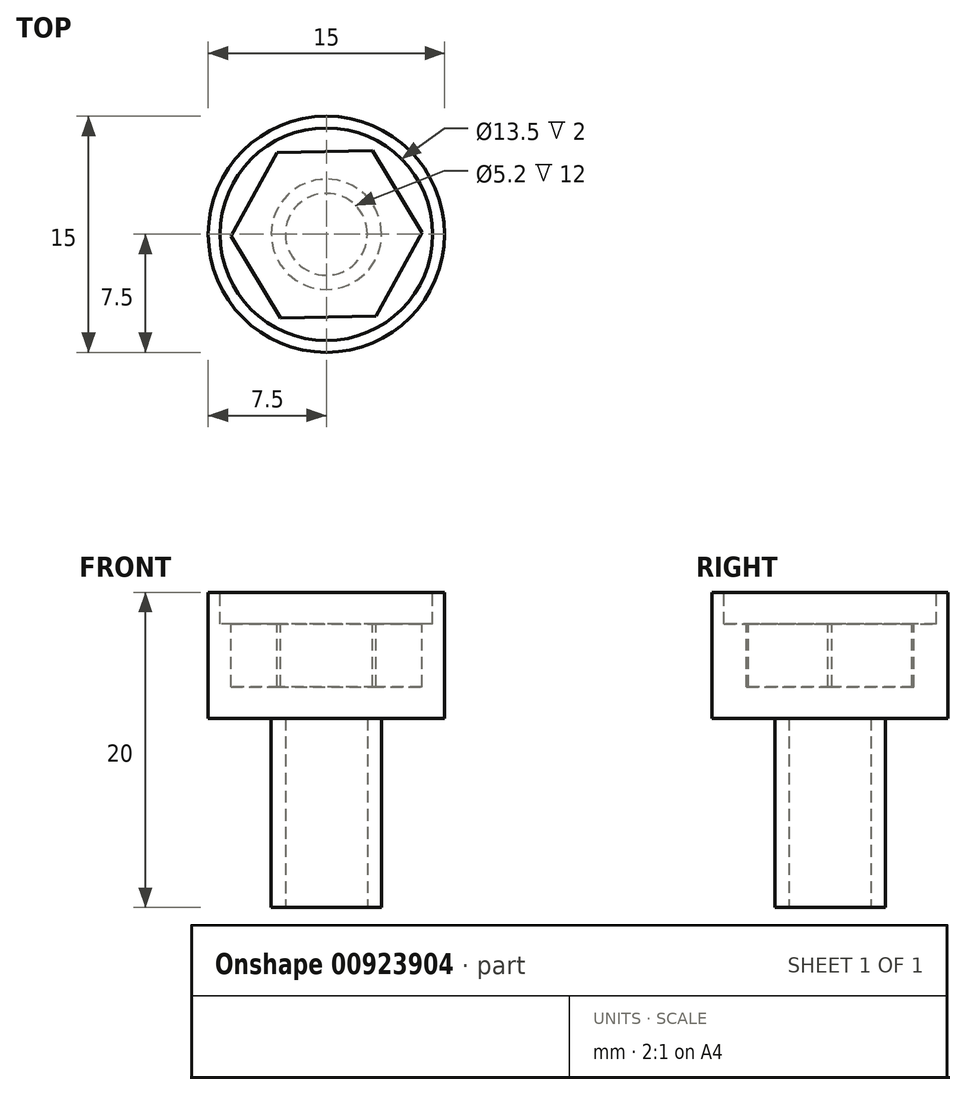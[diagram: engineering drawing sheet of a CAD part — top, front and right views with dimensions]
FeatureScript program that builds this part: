
annotation { "Feature Type Name" : "Feature", "Feature Type Description" : "" }
export const myFeature = defineFeature(function(context is Context, id is Id, definition is map)
    precondition{}
    {
        {
            var Q0;
            Q0=qCreatedBy(makeId("Top.planeOp"),FACE);
            var sketch = newSketch(context, id + "F0", { "sketchPlane" : qUnion([Q0])});
            skCircle(sketch, "E0", {"center": v(0, 0) * mm, "radius": 7.5 * mm});
            skSolve(sketch);
        }
        {
            var Q0;
            Q0=makeQuery(id+"F0.imprint","IMPRINT",FACE,{"disambiguationData":[TD([[makeQuery(id+"F0.imprint","IMPRINT",EDGE,{"derivedFrom":sQuery(id+"F0.wireOp",EDGE,"E0")}),1.0]])]});
            extrude(context, id + "F1", {"entities" : qUnion([Q0]), "depth" : 8 * mm, "offsetDistance" : 25 * mm});
        }
        {
            var Q0;
            Q0=makeQuery(id+"F1.opExtrude","CAP_FACE",FACE,{"disambiguationData":[OSD([sQuery(id+"F0.wireOp",EDGE,"E0")])],"isStart":false});
            var sketch = newSketch(context, id + "F2", { "sketchPlane" : qUnion([Q0])});
            skCircle(sketch, "E1", {"center": v(0, 0) * mm, "radius": 6.75 * mm});
            skSolve(sketch);
        }
        {
            var Q0;
            Q0=makeQuery(id+"F2.imprint","IMPRINT",FACE,{"disambiguationData":[TD([[makeQuery(id+"F2.imprint","IMPRINT",EDGE,{"derivedFrom":sQuery(id+"F2.wireOp",EDGE,"E1")}),1.0]])]});
            extrude(context, id + "F3", {"entities" : qUnion([Q0]), "operationType" : NewBodyOperationType.REMOVE, "oppositeDirection" : true, "depth" : 2 * mm, "offsetDistance" : 25 * mm});
        }
        {
            var Q0;
            Q0=makeQuery(id+"F3.boolean.opBoolean","COPY",FACE,{"derivedFrom":makeQuery(id+"F3.opExtrude","CAP_FACE",FACE,{"disambiguationData":[OSD([sQuery(id+"F2.wireOp",EDGE,"E1")])],"isStart":false})});
            var sketch = newSketch(context, id + "F4", { "sketchPlane" : qUnion([Q0])});
            skCircle(sketch, "E2.cCircle", {"center": v(0, 0) * mm, "radius": 5.25 * mm, "construction": true});
            skLineSegment(sketch, "E2.0", {"start": v(2.92, 5.31) * mm, "end": v(6.06, 0.12) * mm});
            skLineSegment(sketch, "E2.1", {"start": v(6.06, 0.12) * mm, "end": v(3.14, -5.19) * mm});
            skLineSegment(sketch, "E2.2", {"start": v(3.14, -5.19) * mm, "end": v(-2.92, -5.31) * mm});
            skLineSegment(sketch, "E2.3", {"start": v(-2.92, -5.31) * mm, "end": v(-6.06, -0.12) * mm});
            skLineSegment(sketch, "E2.4", {"start": v(-6.06, -0.12) * mm, "end": v(-3.14, 5.19) * mm});
            skLineSegment(sketch, "E2.5", {"start": v(-3.14, 5.19) * mm, "end": v(2.92, 5.31) * mm});
            skPoint(sketch, "E2.0.midPoint", {"position": v(4.5, 2.72) * mm});
            skSolve(sketch);
        }
        {
            var Q0;
            Q0=makeQuery(id+"F4.imprint","IMPRINT",FACE,{"disambiguationData":[TD([[makeQuery(id+"F4.imprint","IMPRINT",EDGE,{"derivedFrom":sQuery(id+"F4.wireOp",EDGE,"E2.0")}),-1.0]])]});
            extrude(context, id + "F5", {"entities" : qUnion([Q0]), "operationType" : NewBodyOperationType.REMOVE, "oppositeDirection" : true, "depth" : 4 * mm, "offsetDistance" : 25 * mm});
        }
        {
            var Q0;
            Q0=makeQuery(id+"F1.opExtrude","CAP_FACE",FACE,{"disambiguationData":[OSD([sQuery(id+"F0.wireOp",EDGE,"E0")])],"isStart":true});
            var sketch = newSketch(context, id + "F6", { "sketchPlane" : qUnion([Q0])});
            skCircle(sketch, "E3", {"center": v(0, 0) * mm, "radius": 3.5 * mm});
            skSolve(sketch);
        }
        {
            var Q0;
            Q0=makeQuery(id+"F6.imprint","IMPRINT",FACE,{"disambiguationData":[TD([[makeQuery(id+"F6.imprint","IMPRINT",EDGE,{"derivedFrom":sQuery(id+"F6.wireOp",EDGE,"E3")}),1.0]])]});
            extrude(context, id + "F7", {"entities" : qUnion([Q0]), "operationType" : NewBodyOperationType.ADD, "depth" : 12 * mm, "offsetDistance" : 25 * mm});
        }
        {
            var Q0;
            Q0=makeQuery(id+"F7.opExtrude","CAP_FACE",FACE,{"disambiguationData":[OSD([sQuery(id+"F6.wireOp",EDGE,"E3")])],"isStart":false});
            var sketch = newSketch(context, id + "F8", { "sketchPlane" : qUnion([Q0])});
            skCircle(sketch, "E4", {"center": v(0, 0) * mm, "radius": 2.6 * mm});
            skSolve(sketch);
        }
        {
            var Q0;
            Q0=makeQuery(id+"F8.imprint","IMPRINT",FACE,{"disambiguationData":[TD([[makeQuery(id+"F8.imprint","IMPRINT",EDGE,{"derivedFrom":sQuery(id+"F8.wireOp",EDGE,"E4")}),1.0]])]});
            extrude(context, id + "F9", {"entities" : qUnion([Q0]), "operationType" : NewBodyOperationType.REMOVE, "oppositeDirection" : true, "depth" : 12 * mm, "offsetDistance" : 25 * mm});
        }
    });
